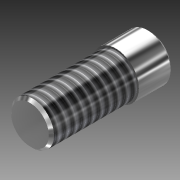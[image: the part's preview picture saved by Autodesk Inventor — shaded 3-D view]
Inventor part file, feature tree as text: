
AUTODESK INVENTOR PART (.ipt)
format: ipt  version: 2011 (Build 150239000, 239)  size: 98,304 bytes
history: native  units: mm (DEFAULTED — no unit token found)
features: extrude x2, chamfer x2, sketch x2, thread x1, reference x1
ambient origin geometry x8: Origin, YZ Plane, XZ Plane, XY Plane, X Axis, Y Axis, Z Axis, Center Point
bodies: Solid1 (feature_tree)
feature tree (8):
  extrude  "Extrusion1"  Depth=5.08mm TaperAngle=0.0deg
  chamfer  "Chamfer1"  Distance=0.381mm
  extrude  "Extrusion2"  Depth=12.7mm TaperAngle=0.0deg
  chamfer  "Chamfer2"  Distance=0.381mm
  thread  "Thread1"  [1 undecoded]
  sketch  "Sketch1"  dims[d0=6.858mm d1=5.08mm d2=0.0mm d3=0.381mm d4=3.175mm]
  reference  "Reference1"
  sketch  "Sketch2"  dims[d5=6.35mm d6=12.7mm d7=0.0mm d8=0.381mm d9=3.175mm d10=25.4mm d11=0.0mm d12=45.0deg d13=45.0deg]
note: 1 required parameter value undecoded (feature->parameter linkage not recoverable at this tier; creation-order binding heuristic only, values carry confidence <= 0.55)
